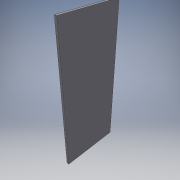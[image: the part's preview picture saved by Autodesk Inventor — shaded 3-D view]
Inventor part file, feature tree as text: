
AUTODESK INVENTOR PART (.ipt)
format: ipt  version: 2016 (Build 200138000, 138)  size: 88,064 bytes
history: native  units: in
note: dims shown in document units (in); Inventor stores cm internally (conversion verified against a paired STEP export)
features: extrude x1, sketch x1
ambient origin geometry x8: Origin, YZ Plane, XZ Plane, XY Plane, X Axis, Y Axis, Z Axis, Center Point
bodies: Solid1 (feature_tree)
feature tree (2):
  extrude  "Extrusion1"  Depth=44.0in
  sketch  "Sketch1"  dims[d0=18.5in d1=44.0in d2=0.75in d3=0.0in]
